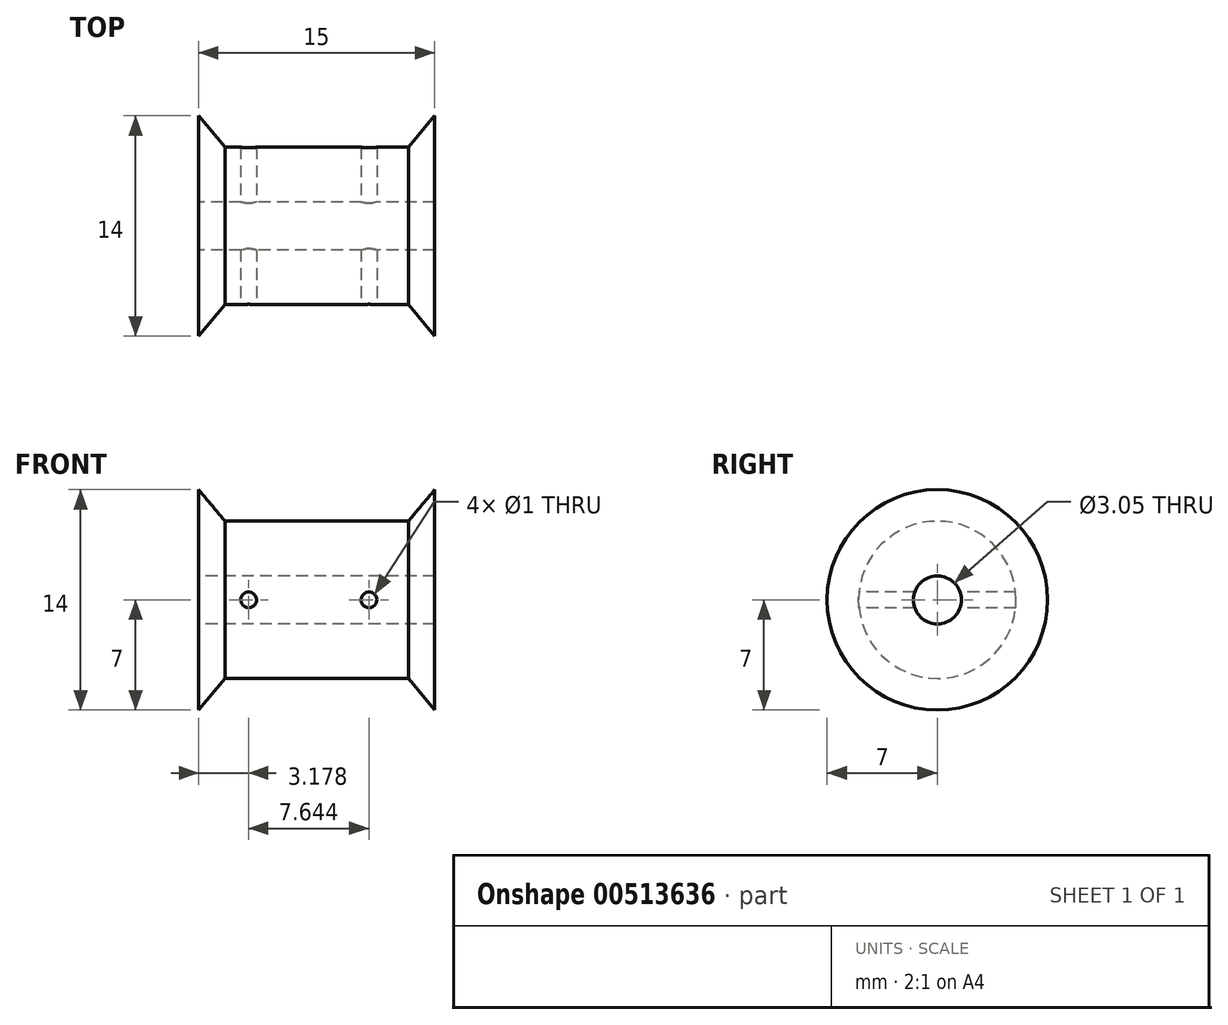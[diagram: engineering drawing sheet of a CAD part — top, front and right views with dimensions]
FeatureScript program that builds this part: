
annotation { "Feature Type Name" : "Feature", "Feature Type Description" : "" }
export const myFeature = defineFeature(function(context is Context, id is Id, definition is map)
    precondition{}
    {
        {
            var Q0;
            Q0=qCreatedBy(makeId("Front.planeOp"),FACE);
            var sketch = newSketch(context, id + "F0", { "sketchPlane" : qUnion([Q0])});
            skLineSegment(sketch, "E0", {"start": v(-23.9, 0) * mm, "end": v(45.16, 0) * mm, "construction": true});
            skLineSegment(sketch, "E1", {"start": v(0, 0) * mm, "end": v(0, 7) * mm});
            skLineSegment(sketch, "E2", {"start": v(0, 7) * mm, "end": v(1.68, 5) * mm});
            skLineSegment(sketch, "E3", {"start": v(1.68, 5) * mm, "end": v(13.32, 5) * mm});
            skLineSegment(sketch, "E4", {"start": v(13.32, 5) * mm, "end": v(15, 7) * mm});
            skLineSegment(sketch, "E5", {"start": v(15, 7) * mm, "end": v(15, 0) * mm});
            skLineSegment(sketch, "E6", {"start": v(0, 1.52) * mm, "end": v(15, 1.52) * mm});
            skSolve(sketch);
        }
        {
            var Q0;
            Q0 = qSketchRegion(id + "F0", true);
            var Q1;
            Q1=sQuery(id+"F0.wireOp",EDGE,"E0");
            revolve(context, id + "F1", {"entities" : qUnion([Q0]), "axis" : qUnion([Q1]), "revolveType" : RevolveType.FULL});
        }
        {
            var Q0;
            Q0=qCreatedBy(makeId("Front.planeOp"),FACE);
            var sketch = newSketch(context, id + "F2", { "sketchPlane" : qUnion([Q0])});
            skCircle(sketch, "E7", {"center": v(3.18, 0) * mm, "radius": 0.5 * mm});
            skCircle(sketch, "E8", {"center": v(10.82, 0) * mm, "radius": 0.5 * mm});
            skSolve(sketch);
        }
        {
            var Q0;
            Q0 = qSketchRegion(id + "F2", true);
            extrude(context, id + "F3", {"entities" : qUnion([Q0]), "operationType" : NewBodyOperationType.REMOVE, "endBound" : BoundingType.THROUGH_ALL, "oppositeDirection" : true, "depth" : 25 * mm, "offsetDistance" : 25 * mm, "hasSecondDirection" : true, "secondDirectionBound" : SecondDirectionBoundingType.THROUGH_ALL, "secondDirectionOppositeDirection" : false, "secondDirectionDepth" : 25 * mm});
        }
    });
